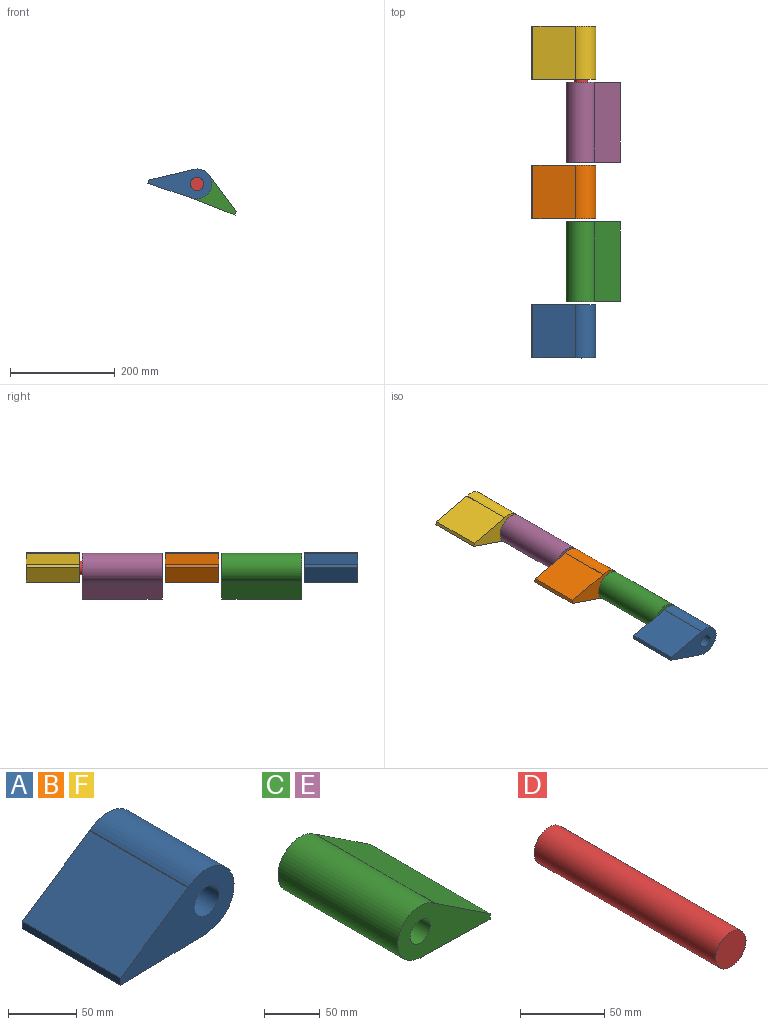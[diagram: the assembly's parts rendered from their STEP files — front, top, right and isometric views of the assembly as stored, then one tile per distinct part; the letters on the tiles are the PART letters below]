
ASSEMBLY  parts=6 mates=13
PART A: 10 faces, bbox 117.4x101.6x59.5 mm
  f0: cylinder r=28.51mm len=101.6mm, axis (0,1,0), area 11161.1mm2, adj f1,f6,f8,f9
  f1: plane 101.6x0.42mm, normal (0,0,1), area 42.3mm2, adj f0,f2,f8,f9
  f2: plane 101.6x69.87mm, normal (-0.55,0,0.83), area 8511.9mm2, adj f1,f3,f8,f9
  f3: plane 101.6x6.35mm, normal (-1,0,0), area 645.2mm2, adj f2,f4,f8,f9
  f4: plane 101.6x85.73mm, normal (0.02,0,-1), area 8711.5mm2, adj f3,f5,f8,f9
  f5: plane 101.6x3.18mm, normal (0,0,-1), area 322.6mm2, adj f4,f6,f8,f9
  f6: plane 101.6x0.7mm, normal (1,0,0), area 71.2mm2, adj f0,f5,f8,f9
  f7: cylinder r=12.7mm len=101.6mm, axis (0,1,0), area 8107.3mm2, adj f8,f9
  f8: plane 117.41x59.51mm, normal (0,-1,0), area 3835.8mm2, adj f0,f1,f2,f3,f4,f5,f6,f7
  f9: plane 117.41x59.51mm, normal (0,1,0), area 3835.8mm2, adj f0,f1,f2,f3,f4,f5,f6,f7
PART B: same geometry as A
PART C: 10 faces, bbox 117.4x152.4x59.5 mm
  f0: plane 152.4x0.42mm, normal (0,0,1), area 63.4mm2, adj f1,f7,f8,f9
  f1: cylinder r=28.51mm len=152.4mm, axis (0,1,0), area 16741.7mm2, adj f0,f2,f8,f9
  f2: plane 152.4x0.7mm, normal (-1,0,0), area 106.8mm2, adj f1,f3,f8,f9
  f3: plane 152.4x3.18mm, normal (0,0,-1), area 483.9mm2, adj f2,f4,f8,f9
  f4: plane 152.4x85.73mm, normal (-0.02,0,-1), area 13067.3mm2, adj f3,f5,f8,f9
  f5: plane 152.4x6.35mm, normal (1,0,0), area 967.7mm2, adj f4,f7,f8,f9
  f6: cylinder r=12.7mm len=152.4mm, axis (0,1,0), area 12161mm2, adj f8,f9
  f7: plane 152.4x69.87mm, normal (0.55,0,0.83), area 12767.9mm2, adj f0,f5,f8,f9
  f8: plane 117.41x59.51mm, normal (0,-1,0), area 3835.8mm2, adj f0,f1,f2,f3,f4,f5,f6,f7
  f9: plane 117.41x59.51mm, normal (0,1,0), area 3835.8mm2, adj f0,f1,f2,f3,f4,f5,f6,f7
PART D: 3 faces, bbox 25.4x152.4x25.4 mm
  f0: cylinder r=12.7mm len=152.4mm, axis (0,1,0), area 12161mm2, adj f1,f2
  f1: plane 25.4x25.4mm, normal (0,-1,0), area 506.7mm2, adj f0
  f2: plane 25.4x25.4mm, normal (0,1,0), area 506.7mm2, adj f0
PART E: same geometry as C
PART F: same geometry as A
PLACE A rot(axis=(0,1,0),20deg) t=(225.55,-1462.52,149.35)mm
PLACE B rot(axis=(0,1,0),20deg) t=(225.55,-1195.82,149.35)mm
PLACE C rot(axis=(0,1,0),20deg) t=(225.55,-1303.77,149.35)mm
PLACE D rot(axis=(0,1,0),20deg) t=(225.55,-929.12,149.35)mm
PLACE E rot(axis=(0,1,0),20deg) t=(225.55,-1037.07,149.35)mm
PLACE F rot(axis=(0,1,0),20deg) t=(225.55,-929.12,149.35)mm
MATE planar B.f4 <-> A.f4  axis (-0.32,0,-0.95) through (185.4,-2262.62,173.64)mm
MATE planar B.f7 <-> C.f1  axis (0,-1,0) through (238.96,-2313.42,186.18)mm
MATE slider F.f7 <-> D.f0  axis (0,1,0) through (238.96,-1945.12,186.18)mm
MATE planar F.f4 <-> B.f4  axis (-0.32,0,-0.95) through (185.4,-1995.92,173.64)mm
MATE planar E.f1 <-> B.f0  axis (0,-1,0) through (238.96,-2205.47,186.18)mm
MATE slider B.f0 <-> D.f0  axis (0,-1,0) through (238.96,-2313.42,186.18)mm
MATE slider A.f7 <-> D.f0  axis (0,1,0) through (238.96,-2529.32,186.18)mm
MATE slider E.f6 <-> D.f0  axis (0,1,0) through (238.96,-2053.07,186.18)mm
MATE slider C.f1 <-> D.f0  axis (0,1,0) through (238.96,-2319.77,186.18)mm
MATE planar F.f7 <-> E.f1  axis (0,-1,0) through (238.96,-2046.72,186.18)mm
MATE planar A.f7 <-> C.f1  axis (0,1,0) through (238.96,-2478.52,186.18)mm
MATE planar D.f0 <-> F.f0  axis (0,1,0) through (238.96,-1945.12,186.18)mm
MATE planar E.f4 <-> C.f4  axis (-0.36,0,-0.93) through (271.92,-2129.27,142.15)mm
